# Revit family: PRD_AR_JntrlUnits_SiriusHingedGrate_ZSIRX001
name_source: partatom
category: Plumbing Fixtures
revit_build: Autodesk Revit 2018 (Build: 20190510_1515(x64)
units: mm (PartAtom-declared; Revit-internal decimal feet)

## family parameters
Always vertical = No
Cut with Voids When Loaded = No
OmniClass Number = 23.45.05.00
OmniClass Title = Sanitary Equipment
Part Type = Normal
Room Calculation Point = No
Round Connector Dimension = Use Diameter
Shared = Yes
Work Plane-Based = No

## types (1)
- ZSIRX001
    AssetType = Fixed
    BIMObjectName = PRD_AR_JanitorialUnits_SiriusHingedGrate_ZSIRX001
    Category = Pr_40_20_96_44, Janitorial sinks
    Color = stainless steel
    Description = Hinged grate (unfixed) of stainless steel to BS313, BS314, LTJ450 and CA210.
    DurationUnit = year
    Features = stainless steel, 4.00 mm, satin finished, bolt mounting, 25x310x430 mm (WxHxD)
    Finish = satin finished
    GrateMaterial = PRD_AR_StainlessSteel_SatinFinished
    GrossWeight = 4.00 kg
    IfcExportAs = IfcFurnitureType
    IfcExportType = NOTDEFINED
    MainColor = stainless steel
    Manufacturer = KWC Group AG
    ManufacturerName = KWC Group AG
    ManufacturerURL = www.kwc.com
    Material = stainless steel 1.4301
    Model = ZSIRX001
    ModelNumber = 2000102678
    ModelReference = ZSIRX001
    NBSDescription = Janitorial units
    NBSReference = 45-35-70/401
    Name = Sirius hinged grate ZSIRX001
    NetWeight = 1.60 kg
    NominalDepth = 310 mm  [stored 1.01706 ft]
    NominalHeight = 0 mm  [stored 0 ft]
    NominalLength = 430 mm
    NominalWidth = 0 mm  [stored 0 ft]
    ProductInformation = https://pim.kwc.com
    Size = 25 x 310 x 430 mm
    Style = Hinged grate
    URL = www.kwc.com
    Uniclass2015Code = Pr_40_20_96_44
    Uniclass2015Title = Janitorial sinks
    Uniclass2015Version = Products v1.5
    Version = 1
    WarrantyDurationUnit = year

note: [stored X ft] marks values corroborated as IEEE doubles in the binary element streams (Revit-internal decimal feet)

## geometry (parser evidence)
native form markers: Sweep x4
no freeform markers — native parametric forms only
